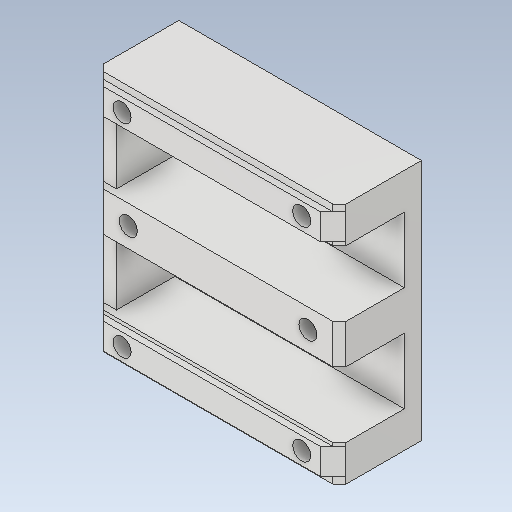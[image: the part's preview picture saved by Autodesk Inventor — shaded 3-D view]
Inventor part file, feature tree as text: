
AUTODESK INVENTOR PART (.ipt)
format: ipt  version: 2020 (Build 240168000, 168)  size: 220,160 bytes
history: native  units: mm
features: extrude x5, sketch x5, chamfer x3, other x2, pattern_linear x1
ambient origin geometry x8: Origin, YZ Plane, XZ Plane, XY Plane, X Axis, Y Axis, Z Axis, Center Point
bodies: Body1 (feature_tree)
feature tree (16):
  other  "Bryła1"
  extrude  "Wyciągnięcie proste1"  Depth=74.0mm
  extrude  "Wyciągnięcie proste2"  Depth=74.0mm
  extrude  "Wyciągnięcie proste3"  Depth=25.0mm TaperAngle=0.0deg
  other  "Płaszczyzna konstrukcyjna1"
  extrude  "Wyciągnięcie proste5"  Depth=20.0mm
  pattern_linear  "Szyk prostokątny1"  Count1=2  [1 undecoded]
  chamfer  "Faza1"  Distance=11.0mm
  chamfer  "Faza2"  Distance=11.0mm
  chamfer  "Faza3"  Distance=19.8mm
  extrude  "Wyciągnięcie proste6"  Depth=2.05mm
  sketch  "Szkic1"
  sketch  "Szkic2"
  sketch  "Szkic3"
  sketch  "Szkic5"
  sketch  "Szkic6"
note: 1 required parameter value undecoded (feature->parameter linkage not recoverable at this tier; creation-order binding heuristic only, values carry confidence <= 0.55)
